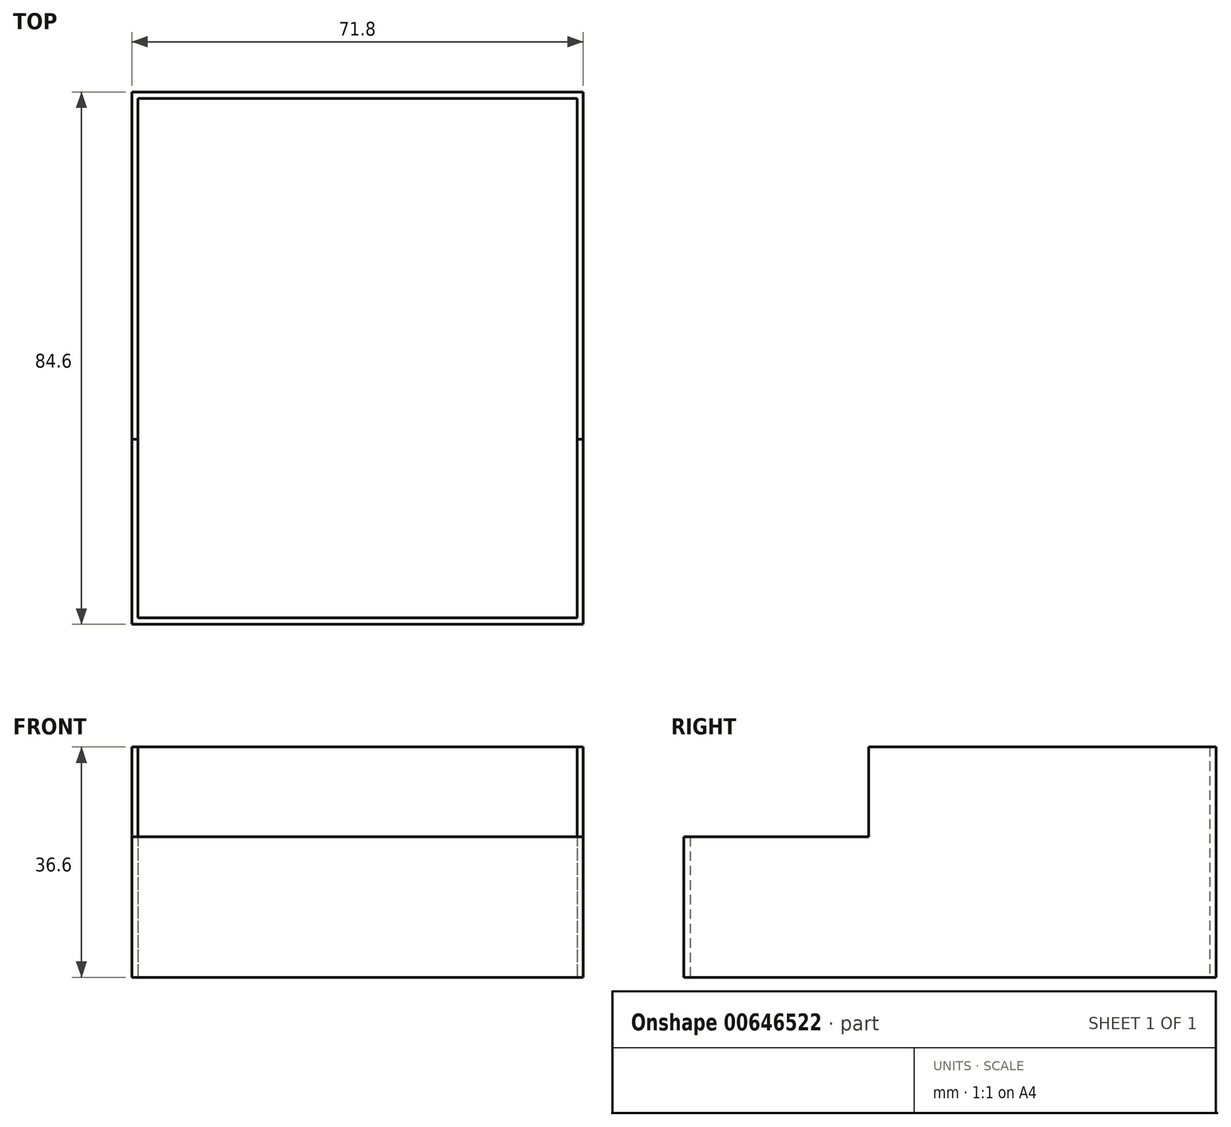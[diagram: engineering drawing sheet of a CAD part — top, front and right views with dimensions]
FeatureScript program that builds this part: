
annotation { "Feature Type Name" : "Feature", "Feature Type Description" : "" }
export const myFeature = defineFeature(function(context is Context, id is Id, definition is map)
    precondition{}
    {
        {
            var Q0;
            Q0=qCreatedBy(makeId("Top.planeOp"),FACE);
            var sketch = newSketch(context, id + "F0", { "sketchPlane" : qUnion([Q0])});
            skLineSegment(sketch, "E0.bottom", {"start": v(35.9, 42.3) * mm, "end": v(-35.9, 42.3) * mm});
            skLineSegment(sketch, "E0.top", {"start": v(35.9, -42.3) * mm, "end": v(-35.9, -42.3) * mm});
            skLineSegment(sketch, "E0.left", {"start": v(35.9, 42.3) * mm, "end": v(35.9, -42.3) * mm});
            skLineSegment(sketch, "E0.right", {"start": v(-35.9, 42.3) * mm, "end": v(-35.9, -42.3) * mm});
            skPoint(sketch, "E0.middle", {"position": v(0, 0) * mm});
            skSolve(sketch);
        }
        {
            var Q0;
            Q0=makeQuery(id+"F0.imprint","IMPRINT",FACE,{"disambiguationData":[TD([[makeQuery(id+"F0.imprint","IMPRINT",EDGE,{"derivedFrom":sQuery(id+"F0.wireOp",EDGE,"E0.bottom")}),1.0]])]});
            var sketch = newSketch(context, id + "F1", { "sketchPlane" : qUnion([Q0])});
            skLineSegment(sketch, "E1.bottom", {"start": v(34.9, 41.3) * mm, "end": v(-34.9, 41.3) * mm});
            skLineSegment(sketch, "E1.top", {"start": v(34.9, -41.3) * mm, "end": v(-34.9, -41.3) * mm});
            skLineSegment(sketch, "E1.left", {"start": v(34.9, 41.3) * mm, "end": v(34.9, -41.3) * mm});
            skLineSegment(sketch, "E1.right", {"start": v(-34.9, 41.3) * mm, "end": v(-34.9, -41.3) * mm});
            skPoint(sketch, "E1.middle", {"position": v(0, 0) * mm});
            skSolve(sketch);
        }
        {
            var Q0;
            Q0 = qSketchRegion(id + "F0", true);
            extrude(context, id + "F2", {"entities" : qUnion([Q0]), "depth" : 36.6 * mm, "offsetDistance" : 25.4 * mm});
        }
        {
            var Q0;
            Q0 = qSketchRegion(id + "F0", true);
            extrude(context, id + "F3", {"entities" : qUnion([Q0]), "operationType" : NewBodyOperationType.ADD, "depth" : 2 * mm, "offsetDistance" : 25.4 * mm});
        }
        {
            var Q0;
            Q0 = qSketchRegion(id + "F1", true);
            extrude(context, id + "F4", {"entities" : qUnion([Q0]), "operationType" : NewBodyOperationType.REMOVE, "depth" : 36.6 * mm, "offsetDistance" : 25.4 * mm});
        }
        {
            var Q0;
            Q0=makeQuery(id+"F2.opExtrude","SWEPT_FACE",FACE,{"disambiguationData":[OSD([sQuery(id+"F0.wireOp",EDGE,"E0.left")])]});
            var sketch = newSketch(context, id + "F5", { "sketchPlane" : qUnion([Q0])});
            skLineSegment(sketch, "E2.bottom", {"start": v(-42.3, 36.6) * mm, "end": v(-12.9, 36.6) * mm});
            skLineSegment(sketch, "E2.top", {"start": v(-42.3, 22.3) * mm, "end": v(-12.9, 22.3) * mm});
            skLineSegment(sketch, "E2.left", {"start": v(-42.3, 36.6) * mm, "end": v(-42.3, 22.3) * mm});
            skLineSegment(sketch, "E2.right", {"start": v(-12.9, 36.6) * mm, "end": v(-12.9, 22.3) * mm});
            skSolve(sketch);
        }
        {
            var Q0;
            Q0 = qSketchRegion(id + "F5", true);
            extrude(context, id + "F6", {"entities" : qUnion([Q0]), "operationType" : NewBodyOperationType.REMOVE, "oppositeDirection" : true, "depth" : 71.8 * mm, "offsetDistance" : 25.4 * mm});
        }
    });
